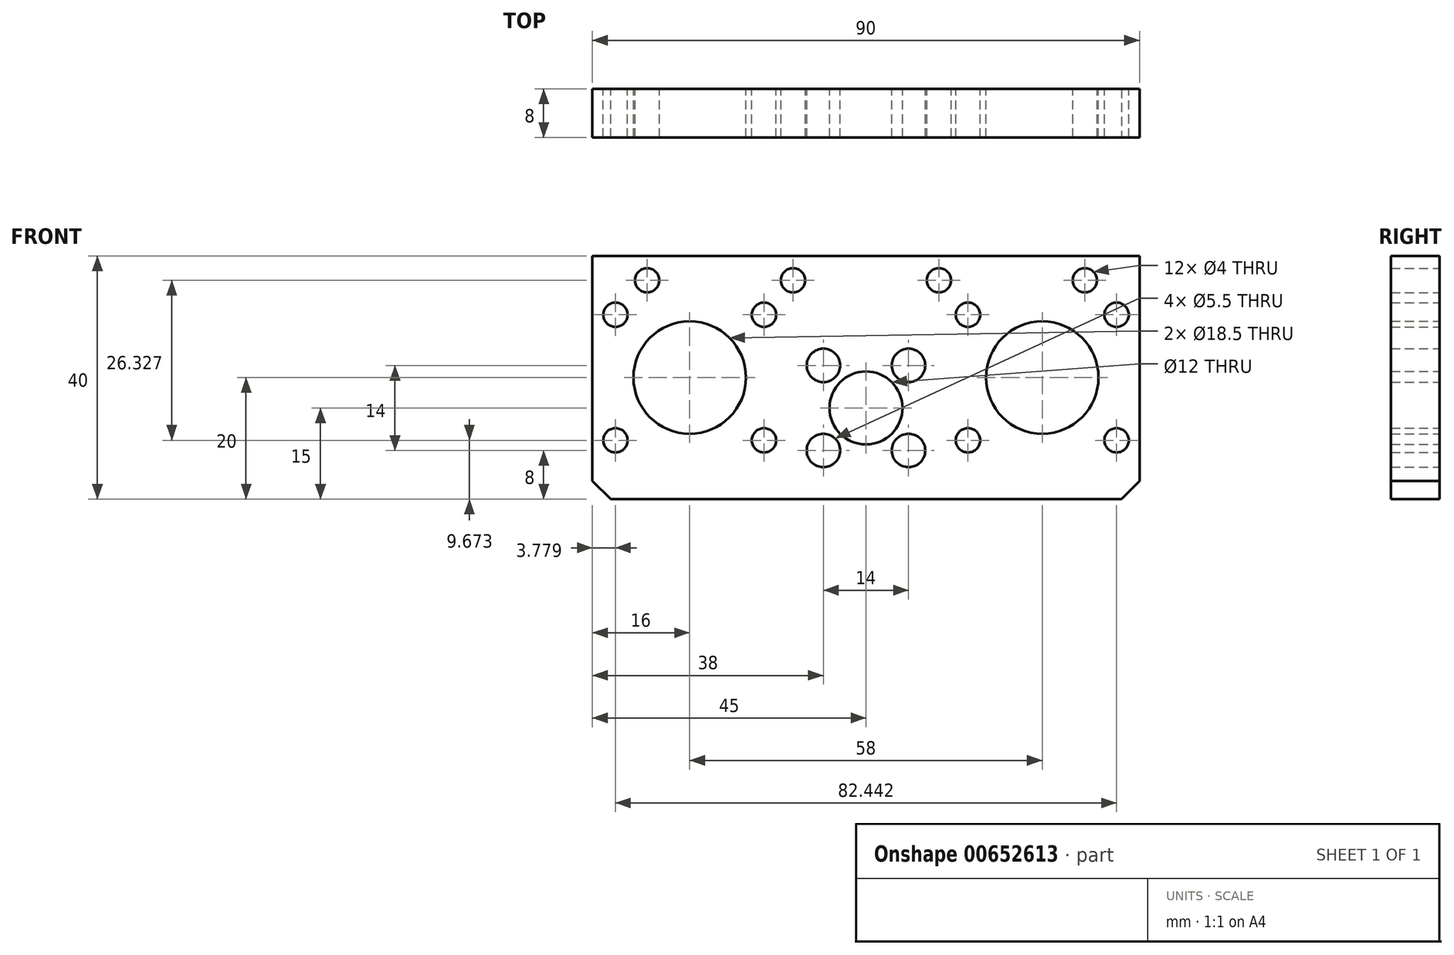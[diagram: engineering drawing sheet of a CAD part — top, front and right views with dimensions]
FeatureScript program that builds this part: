
annotation { "Feature Type Name" : "Feature", "Feature Type Description" : "" }
export const myFeature = defineFeature(function(context is Context, id is Id, definition is map)
    precondition{}
    {
        {
            var Q0;
            Q0=qCreatedBy(makeId("Front.planeOp"),FACE);
            var sketch = newSketch(context, id + "F0", { "sketchPlane" : qUnion([Q0])});
            skLineSegment(sketch, "E0.bottom", {"start": v(0, 0) * mm, "end": v(90, 0) * mm});
            skLineSegment(sketch, "E0.top", {"start": v(0, 40) * mm, "end": v(90, 40) * mm});
            skLineSegment(sketch, "E0.left", {"start": v(0, 0) * mm, "end": v(0, 40) * mm});
            skLineSegment(sketch, "E0.right", {"start": v(90, 0) * mm, "end": v(90, 40) * mm});
            skCircle(sketch, "E1", {"center": v(45, 15) * mm, "radius": 6 * mm});
            skCircle(sketch, "E2", {"center": v(52, 8) * mm, "radius": 2.75 * mm});
            skCircle(sketch, "E3", {"center": v(52, 22) * mm, "radius": 2.75 * mm});
            skCircle(sketch, "E4", {"center": v(38, 22) * mm, "radius": 2.75 * mm});
            skCircle(sketch, "E5", {"center": v(38, 8) * mm, "radius": 2.75 * mm});
            skCircle(sketch, "E6", {"center": v(74, 20) * mm, "radius": 9.25 * mm});
            skCircle(sketch, "E7", {"center": v(16, 20) * mm, "radius": 9.25 * mm});
            skCircle(sketch, "E8", {"center": v(9, 36) * mm, "radius": 2 * mm});
            skCircle(sketch, "E9", {"center": v(33, 36) * mm, "radius": 2 * mm});
            skCircle(sketch, "E10", {"center": v(57, 36) * mm, "radius": 2 * mm});
            skCircle(sketch, "E11", {"center": v(81, 36) * mm, "radius": 2 * mm});
            skCircle(sketch, "E12", {"center": v(3.78, 30.33) * mm, "radius": 2 * mm});
            skCircle(sketch, "E13", {"center": v(3.78, 9.67) * mm, "radius": 2 * mm});
            skCircle(sketch, "E14", {"center": v(28.22, 9.67) * mm, "radius": 2 * mm});
            skCircle(sketch, "E15", {"center": v(28.22, 30.33) * mm, "radius": 2 * mm});
            skCircle(sketch, "E16", {"center": v(61.78, 30.33) * mm, "radius": 2 * mm});
            skCircle(sketch, "E17", {"center": v(61.78, 9.67) * mm, "radius": 2 * mm});
            skCircle(sketch, "E18", {"center": v(86.22, 9.67) * mm, "radius": 2 * mm});
            skCircle(sketch, "E19", {"center": v(86.22, 30.33) * mm, "radius": 2 * mm});
            skSolve(sketch);
        }
        {
            var Q0;
            Q0=makeQuery(id+"F0.imprint","IMPRINT",FACE,{"disambiguationData":[TD([[makeQuery(id+"F0.imprint","IMPRINT",EDGE,{"derivedFrom":sQuery(id+"F0.wireOp",EDGE,"E0.bottom")}),1.0]])]});
            extrude(context, id + "F1", {"entities" : qUnion([Q0]), "depth" : 8 * mm, "offsetDistance" : 25 * mm});
        }
        {
            var Q0;
            Q0=makeQuery(id+"F1.opExtrude","SWEPT_EDGE",EDGE,{"disambiguationData":[OSD([sQuery(id+"F0.wireOp",EDGE,"E0.bottom"),sQuery(id+"F0.wireOp",EDGE,"E0.left")])]});
            var Q1;
            Q1=makeQuery(id+"F1.opExtrude","SWEPT_EDGE",EDGE,{"disambiguationData":[OSD([sQuery(id+"F0.wireOp",EDGE,"E0.bottom"),sQuery(id+"F0.wireOp",EDGE,"E0.right")])]});
            chamfer(context, id + "F2", {"entities" : qUnion([Q0, Q1]), "width" : 3 * mm, "tangentPropagation" : true});
        }
    });
